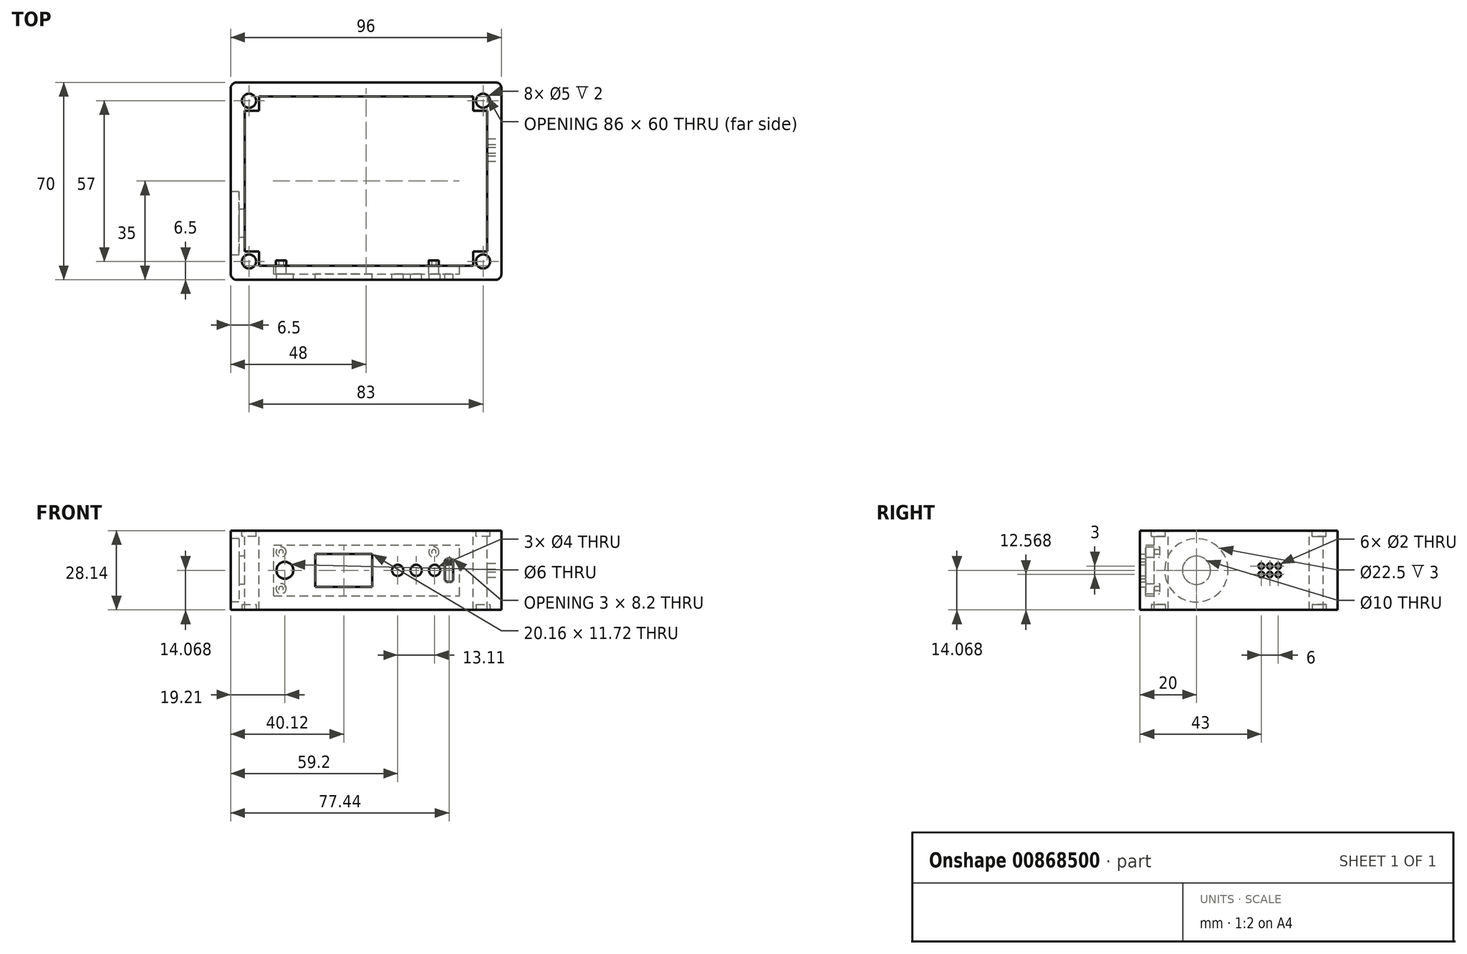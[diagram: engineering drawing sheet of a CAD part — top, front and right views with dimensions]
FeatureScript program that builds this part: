
annotation { "Feature Type Name" : "Feature", "Feature Type Description" : "" }
export const myFeature = defineFeature(function(context is Context, id is Id, definition is map)
    precondition{}
    {
        {
            var Q0;
            Q0=qCreatedBy(makeId("Top.planeOp"),FACE);
            var sketch = newSketch(context, id + "F0", { "sketchPlane" : qUnion([Q0])});
            skLineSegment(sketch, "E0.bottom", {"start": v(-46, 35) * mm, "end": v(46, 35) * mm});
            skLineSegment(sketch, "E0.top", {"start": v(-46, -35) * mm, "end": v(46, -35) * mm});
            skLineSegment(sketch, "E0.left", {"start": v(-48, 33) * mm, "end": v(-48, -33) * mm});
            skLineSegment(sketch, "E0.right", {"start": v(48, 33) * mm, "end": v(48, -33) * mm});
            skPoint(sketch, "E0.middle", {"position": v(0, 0) * mm});
            skPoint(sketch, "E1.visualSharp", {"position": v(-48, 35) * mm});
            skArc(sketch, "E1.filletArc", {"start": v(-46, 35) * mm, "mid": v(-47.41, 34.41) * mm, "end": v(-48, 33) * mm});
            skPoint(sketch, "E2.visualSharp", {"position": v(-48, -35) * mm});
            skArc(sketch, "E2.filletArc", {"start": v(-48, -33) * mm, "mid": v(-47.41, -34.41) * mm, "end": v(-46, -35) * mm});
            skPoint(sketch, "E3.visualSharp", {"position": v(48, -35) * mm});
            skArc(sketch, "E3.filletArc", {"start": v(46, -35) * mm, "mid": v(47.41, -34.41) * mm, "end": v(48, -33) * mm});
            skPoint(sketch, "E4.visualSharp", {"position": v(48, 35) * mm});
            skArc(sketch, "E4.filletArc", {"start": v(48, 33) * mm, "mid": v(47.41, 34.41) * mm, "end": v(46, 35) * mm});
            skSolve(sketch);
        }
        {
            var Q0;
            Q0=makeQuery(id+"F0.imprint","IMPRINT",FACE,{"disambiguationData":[TD([[makeQuery(id+"F0.imprint","IMPRINT",EDGE,{"derivedFrom":sQuery(id+"F0.wireOp",EDGE,"U18dfylj-Norm-gyCY-oxJm-QVkYRqjWbd2D.bottom")}),-1.0]])]});
            var Q1;
            Q1=qSketchRegion(id+"F0",true);
            extrude(context, id + "F1", {"entities" : qUnion([Q0, Q1]), "depth" : 28.14 * mm, "offsetDistance" : 25 * mm});
        }
        {
            var Q0;
            Q0=makeQuery(id+"F1.opExtrude","CAP_FACE",FACE,{"disambiguationData":[OSD([sQuery(id+"F0.wireOp",EDGE,"E0.bottom"),sQuery(id+"F0.wireOp",EDGE,"E0.top"),sQuery(id+"F0.wireOp",EDGE,"E0.left"),sQuery(id+"F0.wireOp",EDGE,"E0.right"),sQuery(id+"F0.wireOp",EDGE,"E1.filletArc"),sQuery(id+"F0.wireOp",EDGE,"E2.filletArc"),sQuery(id+"F0.wireOp",EDGE,"E3.filletArc"),sQuery(id+"F0.wireOp",EDGE,"E4.filletArc")])],"isStart":false});
            var sketch = newSketch(context, id + "F2", { "sketchPlane" : qUnion([Q0])});
            skLineSegment(sketch, "E5.bottom", {"start": v(-44.5, 33) * mm, "end": v(44.5, 33) * mm});
            skLineSegment(sketch, "E5.top", {"start": v(-44.5, -33) * mm, "end": v(44.5, -33) * mm});
            skLineSegment(sketch, "E5.left", {"start": v(-46, 31.5) * mm, "end": v(-46, -31.5) * mm});
            skLineSegment(sketch, "E5.right", {"start": v(46, 31.5) * mm, "end": v(46, -31.5) * mm});
            skPoint(sketch, "E5.middle", {"position": v(0, 0) * mm});
            skPoint(sketch, "E6.visualSharp", {"position": v(-46, 33) * mm});
            skArc(sketch, "E6.filletArc", {"start": v(-44.5, 33) * mm, "mid": v(-45.56, 32.56) * mm, "end": v(-46, 31.5) * mm});
            skPoint(sketch, "E7.visualSharp", {"position": v(46, 33) * mm});
            skArc(sketch, "E7.filletArc", {"start": v(46, 31.5) * mm, "mid": v(45.56, 32.56) * mm, "end": v(44.5, 33) * mm});
            skPoint(sketch, "E8.visualSharp", {"position": v(46, -33) * mm});
            skArc(sketch, "E8.filletArc", {"start": v(44.5, -33) * mm, "mid": v(45.56, -32.56) * mm, "end": v(46, -31.5) * mm});
            skPoint(sketch, "E9.visualSharp", {"position": v(-46, -33) * mm});
            skArc(sketch, "E9.filletArc", {"start": v(-46, -31.5) * mm, "mid": v(-45.56, -32.56) * mm, "end": v(-44.5, -33) * mm});
            skLineSegment(sketch, "E10.bottom", {"start": v(-44, 31.5) * mm, "end": v(44, 31.5) * mm});
            skLineSegment(sketch, "E10.top", {"start": v(-44, -31.5) * mm, "end": v(44, -31.5) * mm});
            skLineSegment(sketch, "E10.left", {"start": v(-44.5, 31) * mm, "end": v(-44.5, -31) * mm});
            skLineSegment(sketch, "E10.right", {"start": v(44.5, 31) * mm, "end": v(44.5, -31) * mm});
            skArc(sketch, "E11.filletArc", {"start": v(-44, 31.5) * mm, "mid": v(-44.35, 31.35) * mm, "end": v(-44.5, 31) * mm});
            skArc(sketch, "E12.filletArc", {"start": v(-44.5, -31) * mm, "mid": v(-44.35, -31.35) * mm, "end": v(-44, -31.5) * mm});
            skArc(sketch, "E13.filletArc", {"start": v(44, -31.5) * mm, "mid": v(44.35, -31.35) * mm, "end": v(44.5, -31) * mm});
            skArc(sketch, "E14.filletArc", {"start": v(44.5, 31) * mm, "mid": v(44.35, 31.35) * mm, "end": v(44, 31.5) * mm});
            skSolve(sketch);
        }
        {
            var Q0;
            Q0=makeQuery(id+"FVReVV0em28uw1l_1.boolean.opBoolean","SPLIT",FACE,{"disambiguationData":[TD([makeQuery(id+"FVReVV0em28uw1l_1.opExtrude","SWEPT_FACE",FACE,{"disambiguationData":[OSD([sQuery(id+"F2.wireOp",EDGE,"E10.bottom")])]})])],"derivedFrom":makeQuery(id+"F1.opExtrude","CAP_FACE",FACE,{"disambiguationData":[OSD([sQuery(id+"F0.wireOp",EDGE,"E0.bottom"),sQuery(id+"F0.wireOp",EDGE,"E0.top"),sQuery(id+"F0.wireOp",EDGE,"E0.left"),sQuery(id+"F0.wireOp",EDGE,"E0.right"),sQuery(id+"F0.wireOp",EDGE,"E1.filletArc"),sQuery(id+"F0.wireOp",EDGE,"E2.filletArc"),sQuery(id+"F0.wireOp",EDGE,"E3.filletArc"),sQuery(id+"F0.wireOp",EDGE,"E4.filletArc")])],"isStart":false})});
            var sketch = newSketch(context, id + "F3", { "sketchPlane" : qUnion([Q0])});
            skCircle(sketch, "E15", {"center": v(-41.5, -28.5) * mm, "radius": 2.5 * mm});
            skCircle(sketch, "E16", {"center": v(-41.5, 28.5) * mm, "radius": 2.5 * mm});
            skCircle(sketch, "E17", {"center": v(41.5, 28.5) * mm, "radius": 2.5 * mm});
            skCircle(sketch, "E18", {"center": v(41.5, -28.5) * mm, "radius": 2.5 * mm});
            skSolve(sketch);
        }
        {
            var Q0;
            Q0=makeQuery(id+"F3.imprint","IMPRINT",FACE,{"disambiguationData":[TD([[makeQuery(id+"F3.imprint","IMPRINT",EDGE,{"derivedFrom":sQuery(id+"F3.wireOp",EDGE,"E15")}),1.0]])]});
            var Q1;
            Q1=makeQuery(id+"F3.imprint","IMPRINT",FACE,{"disambiguationData":[TD([[makeQuery(id+"F3.imprint","IMPRINT",EDGE,{"derivedFrom":sQuery(id+"F3.wireOp",EDGE,"E16")}),1.0]])]});
            var Q2;
            Q2=makeQuery(id+"F3.imprint","IMPRINT",FACE,{"disambiguationData":[TD([[makeQuery(id+"F3.imprint","IMPRINT",EDGE,{"derivedFrom":sQuery(id+"F3.wireOp",EDGE,"E17")}),1.0]])]});
            var Q3;
            Q3=makeQuery(id+"F3.imprint","IMPRINT",FACE,{"disambiguationData":[TD([[makeQuery(id+"F3.imprint","IMPRINT",EDGE,{"derivedFrom":sQuery(id+"F3.wireOp",EDGE,"E18")}),1.0]])]});
            extrude(context, id + "F4", {"entities" : qUnion([Q0, Q1, Q2, Q3]), "operationType" : NewBodyOperationType.REMOVE, "oppositeDirection" : true, "depth" : 2 * mm, "offsetDistance" : 25 * mm});
        }
        {
            var Q0;
            Q0=makeQuery(id+"FVReVV0em28uw1l_1.boolean.opBoolean","SPLIT",FACE,{"disambiguationData":[TD([makeQuery(id+"FVReVV0em28uw1l_1.opExtrude","SWEPT_FACE",FACE,{"disambiguationData":[OSD([sQuery(id+"F2.wireOp",EDGE,"E10.bottom")])]})])],"derivedFrom":makeQuery(id+"F1.opExtrude","CAP_FACE",FACE,{"disambiguationData":[OSD([sQuery(id+"F0.wireOp",EDGE,"E0.bottom"),sQuery(id+"F0.wireOp",EDGE,"E0.top"),sQuery(id+"F0.wireOp",EDGE,"E0.left"),sQuery(id+"F0.wireOp",EDGE,"E0.right"),sQuery(id+"F0.wireOp",EDGE,"E1.filletArc"),sQuery(id+"F0.wireOp",EDGE,"E2.filletArc"),sQuery(id+"F0.wireOp",EDGE,"E3.filletArc"),sQuery(id+"F0.wireOp",EDGE,"E4.filletArc")])],"isStart":false})});
            var sketch = newSketch(context, id + "F5", { "sketchPlane" : qUnion([Q0])});
            skLineSegment(sketch, "E19.bottom", {"start": v(-43, -25) * mm, "end": v(43, -25) * mm});
            skLineSegment(sketch, "E19.top", {"start": v(-43, 25) * mm, "end": v(43, 25) * mm});
            skLineSegment(sketch, "E19.left", {"start": v(-43, -25) * mm, "end": v(-43, 25) * mm});
            skLineSegment(sketch, "E19.right", {"start": v(43, -25) * mm, "end": v(43, 25) * mm});
            skPoint(sketch, "E19.middle", {"position": v(0, 0) * mm});
            skLineSegment(sketch, "E20.bottom", {"start": v(-38, -30) * mm, "end": v(38, -30) * mm});
            skLineSegment(sketch, "E20.top", {"start": v(-38, 30) * mm, "end": v(38, 30) * mm});
            skLineSegment(sketch, "E20.left", {"start": v(-38, -30) * mm, "end": v(-38, 30) * mm});
            skLineSegment(sketch, "E20.right", {"start": v(38, -30) * mm, "end": v(38, 30) * mm});
            skSolve(sketch);
        }
        {
            var Q0;
            {var subQ0=sQuery(id+"F5.wireOp",EDGE,"E19.left");Q0=makeQuery(id+"F5.imprint","IMPRINT",FACE,{"disambiguationData":[TD([[makeQuery(id+"F5.imprint","IMPRINT",EDGE,{"derivedFrom":subQ0}),-1.0]])]});}
            var Q1;
            {var subQ5=sQuery(id+"F5.wireOp",EDGE,"E20.bottom");Q1=makeQuery(id+"F5.imprint","IMPRINT",FACE,{"disambiguationData":[TD([[makeQuery(id+"F5.imprint","IMPRINT",EDGE,{"derivedFrom":subQ5}),1.0]])]});}
            var Q2;
            {var subQ0=sQuery(id+"F5.wireOp",EDGE,"E20.left");var subQ1=sQuery(id+"F5.wireOp",EDGE,"E19.bottom");var subQ2=makeQuery(id+"F5.imprint","INTERSECT",VERTEX,{"derivedFrom":[subQ1,subQ0]});Q2=makeQuery(id+"F5.imprint","IMPRINT",FACE,{"disambiguationData":[TD([[makeQuery(id+"F5.imprint","IMPRINT",EDGE,{"disambiguationData":[TD([[subQ2,-1.0]])],"derivedFrom":subQ1}),1.0]])]});}
            var Q3;
            {var subQ5=sQuery(id+"F5.wireOp",EDGE,"E20.top");Q3=makeQuery(id+"F5.imprint","IMPRINT",FACE,{"disambiguationData":[TD([[makeQuery(id+"F5.imprint","IMPRINT",EDGE,{"derivedFrom":subQ5}),-1.0]])]});}
            var Q4;
            {var subQ0=sQuery(id+"F5.wireOp",EDGE,"E19.right");Q4=makeQuery(id+"F5.imprint","IMPRINT",FACE,{"disambiguationData":[TD([[makeQuery(id+"F5.imprint","IMPRINT",EDGE,{"derivedFrom":subQ0}),1.0]])]});}
            extrude(context, id + "F6", {"entities" : qUnion([Q0, Q1, Q2, Q3, Q4]), "operationType" : NewBodyOperationType.REMOVE, "endBound" : BoundingType.THROUGH_ALL, "oppositeDirection" : true, "depth" : 22 * mm, "offsetDistance" : 25 * mm});
        }
        {
            var Q0;
            Q0=makeQuery(id+"F1.opExtrude","SWEPT_FACE",FACE,{"disambiguationData":[OSD([sQuery(id+"F0.wireOp",EDGE,"E0.right")])]});
            var sketch = newSketch(context, id + "F7", { "sketchPlane" : qUnion([Q0])});
            skPoint(sketch, "E21.centerSnap0", {"position": v(-33, 14.07) * mm});
            skCircle(sketch, "E22", {"center": v(8, 15.57) * mm, "radius": 1 * mm});
            skPoint(sketch, "E22.centerSnap0", {"position": v(0, 0) * mm});
            skCircle(sketch, "E23", {"center": v(11, 15.57) * mm, "radius": 1 * mm});
            skCircle(sketch, "E24", {"center": v(14, 15.57) * mm, "radius": 1 * mm});
            skCircle(sketch, "E25", {"center": v(8, 12.57) * mm, "radius": 1 * mm});
            skCircle(sketch, "E26", {"center": v(11, 12.57) * mm, "radius": 1 * mm});
            skCircle(sketch, "E27", {"center": v(14, 12.57) * mm, "radius": 1 * mm});
            skSolve(sketch);
        }
        {
            var Q0;
            Q0=makeQuery(id+"F7.imprint","IMPRINT",FACE,{"disambiguationData":[TD([[makeQuery(id+"F7.imprint","IMPRINT",EDGE,{"derivedFrom":sQuery(id+"F7.wireOp",EDGE,"E22")}),1.0]])]});
            var Q1;
            Q1=makeQuery(id+"F7.imprint","IMPRINT",FACE,{"disambiguationData":[TD([[makeQuery(id+"F7.imprint","IMPRINT",EDGE,{"derivedFrom":sQuery(id+"F7.wireOp",EDGE,"E25")}),1.0]])]});
            var Q2;
            Q2=makeQuery(id+"F7.imprint","IMPRINT",FACE,{"disambiguationData":[TD([[makeQuery(id+"F7.imprint","IMPRINT",EDGE,{"derivedFrom":sQuery(id+"F7.wireOp",EDGE,"E26")}),1.0]])]});
            var Q3;
            Q3=makeQuery(id+"F7.imprint","IMPRINT",FACE,{"disambiguationData":[TD([[makeQuery(id+"F7.imprint","IMPRINT",EDGE,{"derivedFrom":sQuery(id+"F7.wireOp",EDGE,"E23")}),1.0]])]});
            var Q4;
            Q4=makeQuery(id+"F7.imprint","IMPRINT",FACE,{"disambiguationData":[TD([[makeQuery(id+"F7.imprint","IMPRINT",EDGE,{"derivedFrom":sQuery(id+"F7.wireOp",EDGE,"E24")}),1.0]])]});
            var Q5;
            Q5=makeQuery(id+"F7.imprint","IMPRINT",FACE,{"disambiguationData":[TD([[makeQuery(id+"F7.imprint","IMPRINT",EDGE,{"derivedFrom":sQuery(id+"F7.wireOp",EDGE,"E27")}),1.0]])]});
            extrude(context, id + "F8", {"entities" : qUnion([Q0, Q1, Q2, Q3, Q4, Q5]), "operationType" : NewBodyOperationType.REMOVE, "endBound" : BoundingType.UP_TO_NEXT, "oppositeDirection" : true, "depth" : 25 * mm, "offsetDistance" : 25 * mm});
        }
        {
            var Q0;
            Q0=makeQuery(id+"F1.opExtrude","SWEPT_FACE",FACE,{"disambiguationData":[OSD([sQuery(id+"F0.wireOp",EDGE,"E0.left")])]});
            var sketch = newSketch(context, id + "F9", { "sketchPlane" : qUnion([Q0])});
            skCircle(sketch, "E28", {"center": v(15, 14.07) * mm, "radius": 5 * mm});
            skCircle(sketch, "E29", {"center": v(15, 14.07) * mm, "radius": 11.25 * mm});
            skSolve(sketch);
        }
        {
            var Q0;
            Q0=makeQuery(id+"F9.imprint","IMPRINT",FACE,{"disambiguationData":[TD([[makeQuery(id+"F9.imprint","IMPRINT",EDGE,{"derivedFrom":sQuery(id+"F9.wireOp",EDGE,"E28")}),-1.0]])]});
            extrude(context, id + "F10", {"entities" : qUnion([Q0]), "operationType" : NewBodyOperationType.REMOVE, "oppositeDirection" : true, "depth" : 3 * mm, "offsetDistance" : 25 * mm});
        }
        {
            var Q0;
            Q0=makeQuery(id+"F9.imprint","IMPRINT",FACE,{"disambiguationData":[TD([[makeQuery(id+"F9.imprint","IMPRINT",EDGE,{"derivedFrom":sQuery(id+"F9.wireOp",EDGE,"E28")}),1.0]])]});
            extrude(context, id + "F11", {"entities" : qUnion([Q0]), "operationType" : NewBodyOperationType.REMOVE, "endBound" : BoundingType.UP_TO_NEXT, "oppositeDirection" : true, "depth" : 25 * mm, "offsetDistance" : 25 * mm});
        }
        {
            var Q0;
            Q0=makeQuery(id+"F6.boolean.opBoolean","COPY",FACE,{"derivedFrom":makeQuery(id+"F6.opExtrude","SWEPT_FACE",FACE,{"disambiguationData":[OSD([sQuery(id+"F5.wireOp",EDGE,"E20.bottom")])]})});
            var sketch = newSketch(context, id + "F12", { "sketchPlane" : qUnion([Q0])});
            skLineSegment(sketch, "E30.bottom", {"start": v(32.79, 5.07) * mm, "end": v(-33.21, 5.07) * mm});
            skLineSegment(sketch, "E30.top", {"start": v(32.79, 23.07) * mm, "end": v(-33.21, 23.07) * mm});
            skLineSegment(sketch, "E30.left", {"start": v(32.79, 5.07) * mm, "end": v(32.79, 23.07) * mm});
            skLineSegment(sketch, "E30.right", {"start": v(-33.21, 5.07) * mm, "end": v(-33.21, 23.07) * mm});
            skPoint(sketch, "E30.middle", {"position": v(-0.21, 14.07) * mm});
            skPoint(sketch, "E30.middle.positionSnap0", {"position": v(45.84, 14.07) * mm});
            skPoint(sketch, "E30.centerSnap0", {"position": v(45.84, 14.07) * mm});
            skLineSegment(sketch, "E31.bottom", {"start": v(-29.94, 9.97) * mm, "end": v(-28.94, 9.97) * mm});
            skLineSegment(sketch, "E31.top", {"start": v(-29.94, 18.17) * mm, "end": v(-28.94, 18.17) * mm});
            skLineSegment(sketch, "E31.left", {"start": v(-30.94, 10.97) * mm, "end": v(-30.94, 17.17) * mm});
            skLineSegment(sketch, "E31.right", {"start": v(-27.94, 10.97) * mm, "end": v(-27.94, 17.17) * mm});
            skPoint(sketch, "E31.middle", {"position": v(-29.44, 14.07) * mm});
            skPoint(sketch, "E31.middle.positionSnap0", {"position": v(-33.21, 14.07) * mm});
            skPoint(sketch, "E31.centerSnap0", {"position": v(-33.21, 14.07) * mm});
            skPoint(sketch, "E32.visualSharp", {"position": v(-27.94, 18.17) * mm});
            skArc(sketch, "E32.filletArc", {"start": v(-27.94, 17.17) * mm, "mid": v(-28.23, 17.87) * mm, "end": v(-28.94, 18.17) * mm});
            skPoint(sketch, "E33.visualSharp", {"position": v(-27.94, 9.97) * mm});
            skArc(sketch, "E33.filletArc", {"start": v(-28.94, 9.97) * mm, "mid": v(-28.23, 10.26) * mm, "end": v(-27.94, 10.97) * mm});
            skPoint(sketch, "E34.visualSharp", {"position": v(-30.94, 9.97) * mm});
            skArc(sketch, "E34.filletArc", {"start": v(-30.94, 10.97) * mm, "mid": v(-30.65, 10.26) * mm, "end": v(-29.94, 9.97) * mm});
            skPoint(sketch, "E35.visualSharp", {"position": v(-30.94, 18.17) * mm});
            skArc(sketch, "E35.filletArc", {"start": v(-29.94, 18.17) * mm, "mid": v(-30.65, 17.87) * mm, "end": v(-30.94, 17.17) * mm});
            skCircle(sketch, "E36", {"center": v(-24.31, 14.07) * mm, "radius": 2 * mm});
            skCircle(sketch, "E37", {"center": v(-17.76, 14.07) * mm, "radius": 2 * mm});
            skCircle(sketch, "E38", {"center": v(-11.2, 14.07) * mm, "radius": 2 * mm});
            skCircle(sketch, "E39", {"center": v(28.79, 14.07) * mm, "radius": 3 * mm});
            skCircle(sketch, "E40", {"center": v(30.13, 20.57) * mm, "radius": 1.8 * mm});
            skCircle(sketch, "E41", {"center": v(30.13, 20.57) * mm, "radius": 0.8 * mm});
            skCircle(sketch, "E42", {"center": v(30.13, 7.57) * mm, "radius": 1.8 * mm});
            skCircle(sketch, "E43", {"center": v(30.13, 7.57) * mm, "radius": 0.8 * mm});
            skLineSegment(sketch, "E44.bottom", {"start": v(-2.2, 19.93) * mm, "end": v(17.96, 19.93) * mm});
            skLineSegment(sketch, "E44.top", {"start": v(-2.2, 8.2) * mm, "end": v(17.96, 8.2) * mm});
            skLineSegment(sketch, "E44.left", {"start": v(-2.2, 19.93) * mm, "end": v(-2.2, 8.2) * mm});
            skLineSegment(sketch, "E44.right", {"start": v(17.96, 19.93) * mm, "end": v(17.96, 8.2) * mm});
            skPoint(sketch, "E44.middle", {"position": v(7.88, 14.07) * mm});
            skCircle(sketch, "E45", {"center": v(-24.05, 20.57) * mm, "radius": 1.8 * mm});
            skCircle(sketch, "E46", {"center": v(-24.05, 20.57) * mm, "radius": 0.8 * mm});
            skSolve(sketch);
        }
        {
            var Q0;
            Q0=makeQuery(id+"F12.imprint","IMPRINT",FACE,{"disambiguationData":[TD([[makeQuery(id+"F12.imprint","IMPRINT",EDGE,{"derivedFrom":sQuery(id+"F12.wireOp",EDGE,"E44.bottom")}),-1.0]])]});
            var Q1;
            Q1=makeQuery(id+"F12.imprint","IMPRINT",FACE,{"disambiguationData":[TD([[makeQuery(id+"F12.imprint","IMPRINT",EDGE,{"derivedFrom":sQuery(id+"F12.wireOp",EDGE,"E39")}),1.0]])]});
            var Q2;
            Q2=makeQuery(id+"F12.imprint","IMPRINT",FACE,{"disambiguationData":[TD([[makeQuery(id+"F12.imprint","IMPRINT",EDGE,{"derivedFrom":sQuery(id+"F12.wireOp",EDGE,"E38")}),1.0]])]});
            var Q3;
            Q3=makeQuery(id+"F12.imprint","IMPRINT",FACE,{"disambiguationData":[TD([[makeQuery(id+"F12.imprint","IMPRINT",EDGE,{"derivedFrom":sQuery(id+"F12.wireOp",EDGE,"E37")}),1.0]])]});
            var Q4;
            Q4=makeQuery(id+"F12.imprint","IMPRINT",FACE,{"disambiguationData":[TD([[makeQuery(id+"F12.imprint","IMPRINT",EDGE,{"derivedFrom":sQuery(id+"F12.wireOp",EDGE,"E36")}),1.0]])]});
            var Q5;
            Q5=makeQuery(id+"F12.imprint","IMPRINT",FACE,{"disambiguationData":[TD([[makeQuery(id+"F12.imprint","IMPRINT",EDGE,{"derivedFrom":sQuery(id+"F12.wireOp",EDGE,"E31.bottom")}),1.0]])]});
            extrude(context, id + "F13", {"entities" : qUnion([Q0, Q1, Q2, Q3, Q4, Q5]), "operationType" : NewBodyOperationType.REMOVE, "endBound" : BoundingType.UP_TO_NEXT, "oppositeDirection" : true, "depth" : 25 * mm, "offsetDistance" : 25 * mm});
        }
        {
            var Q0;
            Q0=makeQuery(id+"F12.imprint","IMPRINT",FACE,{"disambiguationData":[TD([[makeQuery(id+"F12.imprint","IMPRINT",EDGE,{"derivedFrom":sQuery(id+"F12.wireOp",EDGE,"E30.bottom")}),-1.0]])]});
            extrude(context, id + "F14", {"entities" : qUnion([Q0]), "operationType" : NewBodyOperationType.REMOVE, "oppositeDirection" : true, "depth" : -3 * mm, "offsetDistance" : 25 * mm});
        }
        {
            var Q0;
            Q0=makeQuery(id+"F12.imprint","IMPRINT",FACE,{"disambiguationData":[TD([[makeQuery(id+"F12.imprint","IMPRINT",EDGE,{"derivedFrom":sQuery(id+"F12.wireOp",EDGE,"E30.bottom")}),-1.0]])]});
            extrude(context, id + "F15", {"entities" : qUnion([Q0]), "operationType" : NewBodyOperationType.REMOVE, "oppositeDirection" : true, "depth" : 3 * mm, "offsetDistance" : 25 * mm});
        }
        {
            var Q0;
            Q0=makeQuery(id+"F12.imprint","IMPRINT",FACE,{"disambiguationData":[TD([[makeQuery(id+"F12.imprint","IMPRINT",EDGE,{"derivedFrom":sQuery(id+"F12.wireOp",EDGE,"E40")}),1.0]])]});
            var Q1;
            Q1=sQuery(id+"F12.wireOp",EDGE,"E41");
            var Q2;
            Q2=sQuery(id+"F12.wireOp",EDGE,"E40");
            extrude(context, id + "F16", {"entities" : qUnion([Q0]), "operationType" : NewBodyOperationType.ADD, "surfaceEntities" : qUnion([Q1, Q2]), "depth" : 1.9 * mm, "offsetDistance" : 25 * mm});
        }
        {
            var Q0;
            Q0=makeQuery(id+"F12.imprint","IMPRINT",FACE,{"disambiguationData":[TD([[makeQuery(id+"F12.imprint","IMPRINT",EDGE,{"derivedFrom":sQuery(id+"F12.wireOp",EDGE,"E42")}),1.0]])]});
            var Q1;
            Q1=sQuery(id+"F12.wireOp",EDGE,"E43");
            var Q2;
            Q2=sQuery(id+"F12.wireOp",EDGE,"E42");
            extrude(context, id + "F17", {"entities" : qUnion([Q0]), "operationType" : NewBodyOperationType.ADD, "surfaceEntities" : qUnion([Q1, Q2]), "depth" : 1.9 * mm, "offsetDistance" : 25 * mm});
        }
        {
            var Q0;
            Q0=makeQuery(id+"F12.imprint","IMPRINT",FACE,{"disambiguationData":[TD([[makeQuery(id+"F12.imprint","IMPRINT",EDGE,{"derivedFrom":sQuery(id+"F12.wireOp",EDGE,"E45")}),1.0]])]});
            extrude(context, id + "F18", {"entities" : qUnion([Q0]), "operationType" : NewBodyOperationType.ADD, "depth" : 1.9 * mm, "offsetDistance" : 25 * mm});
        }
        {
            var Q0;
            Q0=makeQuery(id+"F1.opExtrude","CAP_FACE",FACE,{"disambiguationData":[OSD([sQuery(id+"F0.wireOp",EDGE,"E0.bottom"),sQuery(id+"F0.wireOp",EDGE,"E0.top"),sQuery(id+"F0.wireOp",EDGE,"E0.left"),sQuery(id+"F0.wireOp",EDGE,"E0.right"),sQuery(id+"F0.wireOp",EDGE,"E1.filletArc"),sQuery(id+"F0.wireOp",EDGE,"E2.filletArc"),sQuery(id+"F0.wireOp",EDGE,"E3.filletArc"),sQuery(id+"F0.wireOp",EDGE,"E4.filletArc")])],"isStart":true});
            var sketch = newSketch(context, id + "F19", { "sketchPlane" : qUnion([Q0])});
            skCircle(sketch, "E47", {"center": v(-41.5, -28.5) * mm, "radius": 2.5 * mm});
            skCircle(sketch, "E48", {"center": v(-41.5, 28.5) * mm, "radius": 2.5 * mm});
            skCircle(sketch, "E49", {"center": v(41.5, -28.5) * mm, "radius": 2.5 * mm});
            skCircle(sketch, "E50", {"center": v(41.5, 28.5) * mm, "radius": 2.5 * mm});
            skSolve(sketch);
        }
        {
            var Q0;
            Q0=makeQuery(id+"F19.imprint","IMPRINT",FACE,{"disambiguationData":[TD([[makeQuery(id+"F19.imprint","IMPRINT",EDGE,{"derivedFrom":sQuery(id+"F19.wireOp",EDGE,"E47")}),1.0]])]});
            var Q1;
            Q1=makeQuery(id+"F19.imprint","IMPRINT",FACE,{"disambiguationData":[TD([[makeQuery(id+"F19.imprint","IMPRINT",EDGE,{"derivedFrom":sQuery(id+"F19.wireOp",EDGE,"E48")}),1.0]])]});
            var Q2;
            Q2=makeQuery(id+"F19.imprint","IMPRINT",FACE,{"disambiguationData":[TD([[makeQuery(id+"F19.imprint","IMPRINT",EDGE,{"derivedFrom":sQuery(id+"F19.wireOp",EDGE,"E49")}),1.0]])]});
            var Q3;
            Q3=makeQuery(id+"F19.imprint","IMPRINT",FACE,{"disambiguationData":[TD([[makeQuery(id+"F19.imprint","IMPRINT",EDGE,{"derivedFrom":sQuery(id+"F19.wireOp",EDGE,"E50")}),1.0]])]});
            var Q4;
            Q4=sQuery(id+"F19.wireOp",EDGE,"E47");
            var Q5;
            Q5=sQuery(id+"F19.wireOp",EDGE,"E48");
            var Q6;
            Q6=sQuery(id+"F19.wireOp",EDGE,"E49");
            var Q7;
            Q7=sQuery(id+"F19.wireOp",EDGE,"E50");
            extrude(context, id + "F20", {"entities" : qUnion([Q0, Q1, Q2, Q3]), "operationType" : NewBodyOperationType.REMOVE, "surfaceEntities" : qUnion([Q4, Q5, Q6, Q7]), "oppositeDirection" : true, "depth" : 2 * mm, "offsetDistance" : 25 * mm});
        }
    });
